# Revit family: LAMP_PUZZLE TR FRAME
name_source: partatom
category: Modelos genéricos
revit_build: Autodesk Revit 2015 (Build: 20140606_1530(x64)
units: mm (PartAtom-declared; Revit-internal decimal feet)

## types (14) — shared parameters
Accessory Type = Assembly
Comentarios de tipo = Availability of changing between standard frame Types when placed in a project.
Elevación por defecto = 1219 mm
Fabricante = LAMP
Installation instructions = http://www.lamp.es
Last update = 25/07/2018
Manufacturer URL = http://www.lamp.es
Manufacturer country = Spain
Manufacturer name = LAMP
Model explanation = Availability of changing between standard frame Types when placed in a project.
Product datasheet = http://www.lamp.es

## per-type parameters (varying)
| type | Descripción | Dimensions | Dist. A Exterior | Dist. B Exterior | Finish | Material marco | Modelo | Product code | Recessed dimensions | Weight |
| TYPE 1 BLACK | PUZZLE ACC. HIDDEN FRAME Nº1 BK. | 186 x 186 | 186 mm  [stored 0.610236 ft] | 186 mm  [stored 0.610236 ft] | Shiny black | LAMP_Aluminio frame Puzzle BL | PUTRFR1B | PUTRFR1B | 174 x 174 | 0.27 kg |
| TYPE 1 WHITE | PUZZLE ACC. HIDDEN FRAME Nº1 WH. | 186 x 186 | 186 mm  [stored 0.610236 ft] | 186 mm  [stored 0.610236 ft] | Shiny white | LAMP_Aluminio frame Puzzle WH | PUTRFR1W | PUTRFR1W | 174 x 174 | 0.27 kg |
| TYPE 2 BLACK | PUZZLE ACC. HIDDEN FRAME Nº2 BK. | 344 x 190 | 344 mm  [stored 1.12861 ft] | 190 mm | Shiny black | LAMP_Aluminio frame Puzzle BL | PUTRFR2B | PUTRFR2B | 332 x 178 | 0.46 kg |
| TYPE 2 WHITE | PUZZLE ACC. HIDDEN FRAME Nº2 WH. | 344 x 190 | 344 mm  [stored 1.12861 ft] | 190 mm | Shiny white | LAMP_Aluminio frame Puzzle WH | PUTRFR2W | PUTRFR2W | 332 x 178 | 0.45 kg |
| TYPE 3 BLACK | PUZZLE ACC. HIDDEN FRAME Nº3 BK. | 494 x 190 | 494 mm | 190 mm | Shiny black | LAMP_Aluminio frame Puzzle BL | PUTRFR3B | PUTRFR3B | 482 x 178 | 0.58 kg |
| TYPE 3 WHITE | PUZZLE ACC. HIDDEN FRAME Nº3 WH. | 494 x 190 | 494 mm | 190 mm | Shiny white | LAMP_Aluminio frame Puzzle WH | PUTRFR3W | PUTRFR3W | 482 x 178 | 0.70 kg |
| TYPE 4 BLACK | PUZZLE ACC. HIDDEN FRAME Nº4 BK. | 654 x 190 | 654 mm | 190 mm | Shiny black | LAMP_Aluminio frame Puzzle BL | PUTRFR4B | PUTRFR4B | 642 x 178 | 0.60 kg |
| TYPE 4 WHITE | PUZZLE ACC. HIDDEN FRAME Nº4 WH. | 654 x 190 | 654 mm | 190 mm | Shiny white | LAMP_Aluminio frame Puzzle WH | PUTRFR4W | PUTRFR4W | 642 x 178 | 0.94 kg |
| TYPE 5 BLACK | PUZZLE ACC. HIDDEN FRAME Nº5 BK. | 959 x 190 | 959 mm  [stored 3.14633 ft] | 190 mm | Shiny black | LAMP_Aluminio frame Puzzle BL | PUTRFR5B | PUTRFR5B | 974 x 178 | 0.94 kg |
| TYPE 5 WHITE | PUZZLE ACC. HIDDEN FRAME Nº5 WH. | 959 x 190 | 959 mm  [stored 3.14633 ft] | 190 mm | Shiny white | LAMP_Aluminio frame Puzzle WH | PUTRFR5W | PUTRFR5W | 974 x 178 | 0.94 kg |
| TYPE 6 BLACK | PUZZLE ACC. HIDDEN FRAME Nº6 BK. | 1264 x 190 | 1264 mm | 190 mm | Shiny black | LAMP_Aluminio frame Puzzle BL | PUTRFR6B | PUTRFR6B | 1252 x 178 | 1.17 kg |
| TYPE 6 WHITE | PUZZLE ACC. HIDDEN FRAME Nº6 WH. | 1264 x 190 | 1264 mm | 190 mm | Shiny white | LAMP_Aluminio frame Puzzle WH | PUTRFR6W | PUTRFR6W | 1252 x 178 | 1.18 kg |
| TYPE 9 BLACK | PUZZLE ACC. HIDDEN FRAME Nº9 BK. | 344 x 344 | 344 mm  [stored 1.12861 ft] | 344 mm  [stored 1.12861 ft] | Shiny black | LAMP_Aluminio frame Puzzle BL | PUTRFR9B | PUTRFR9B | 332 x 332 | 0.58 kg |
| TYPE 9 WHITE | PUZZLE ACC. HIDDEN FRAME Nº9 WH. | 344 x 344 | 344 mm  [stored 1.12861 ft] | 344 mm  [stored 1.12861 ft] | Shiny white | LAMP_Aluminio frame Puzzle WH | PUTRFR9W | PUTRFR9W | 332 x 332 | 0.60 kg |

note: [stored X ft] marks values corroborated as IEEE doubles in the binary element streams (Revit-internal decimal feet)
